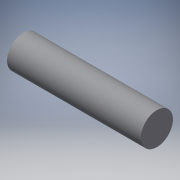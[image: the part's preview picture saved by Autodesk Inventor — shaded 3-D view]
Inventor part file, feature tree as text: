
AUTODESK INVENTOR PART (.ipt)
format: ipt  version: 2019 (Build 230136000, 136)  size: 93,696 bytes
history: native  units: in
note: dims shown in document units (in); Inventor stores cm internally (conversion verified against a paired STEP export)
features: revolve x1, sketch x1
ambient origin geometry x8: Origin, YZ Plane, XZ Plane, XY Plane, X Axis, Y Axis, Z Axis, Center Point
bodies: Solid1 (feature_tree)
feature tree (2):
  revolve  "Revolution1"  [1 undecoded]
  sketch  "Sketch1"  dims[d0=0.7874in d1=0.0945in d12=90.0deg]
note: 1 required parameter value undecoded (feature->parameter linkage not recoverable at this tier; creation-order binding heuristic only, values carry confidence <= 0.55)
